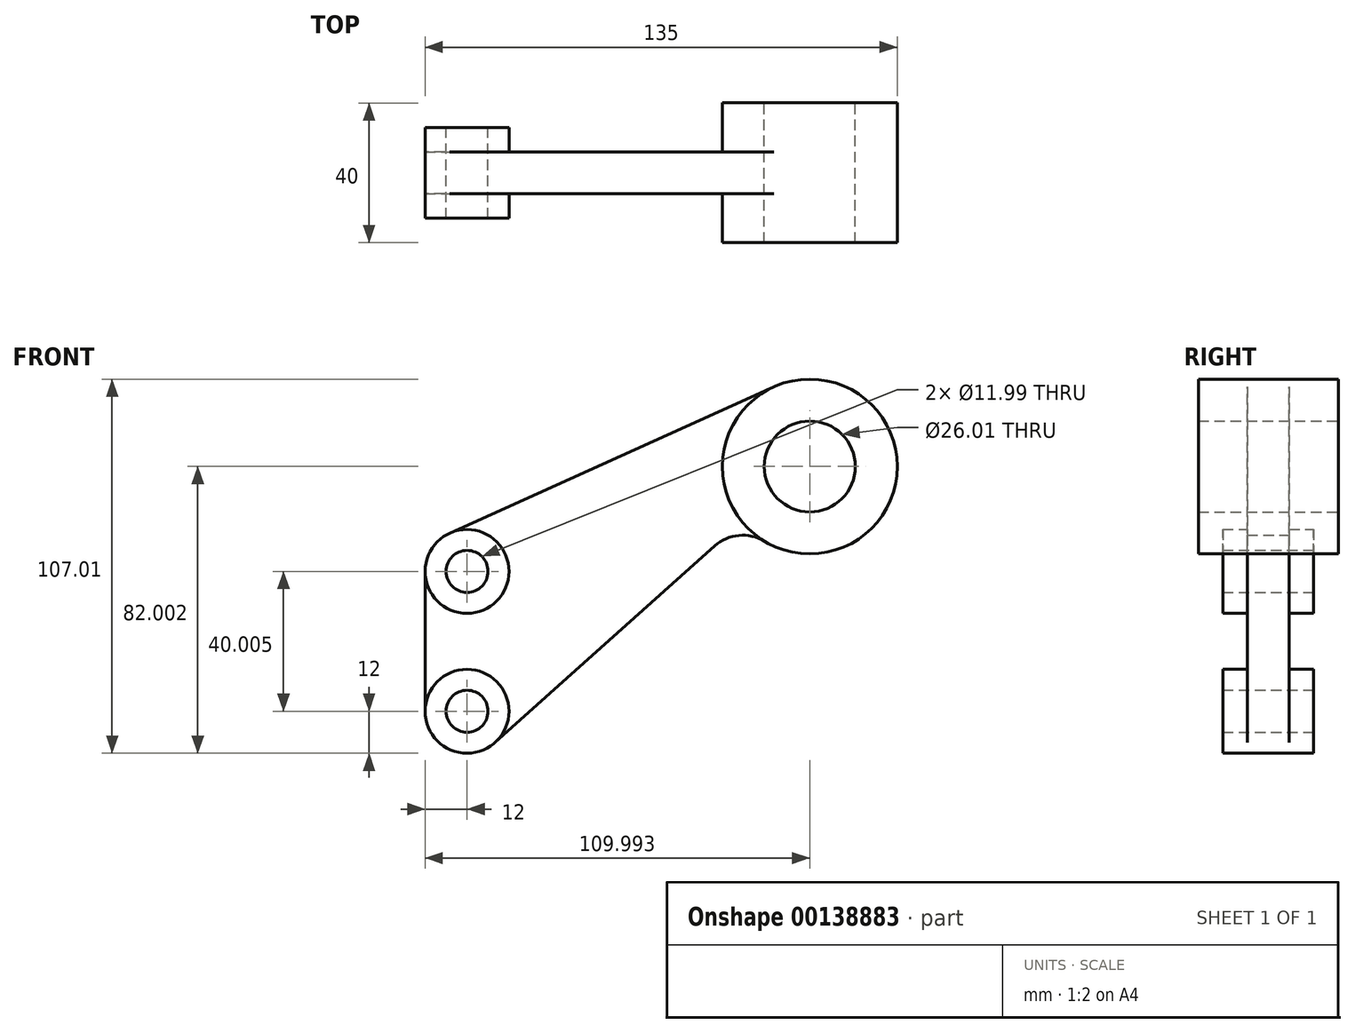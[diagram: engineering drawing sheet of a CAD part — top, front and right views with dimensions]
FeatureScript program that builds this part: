
annotation { "Feature Type Name" : "Feature", "Feature Type Description" : "" }
export const myFeature = defineFeature(function(context is Context, id is Id, definition is map)
    precondition{}
    {
        {
            var Q0;
            Q0=qCreatedBy(makeId("Front.planeOp"),FACE);
            var sketch = newSketch(context, id + "F0", { "sketchPlane" : qUnion([Q0])});
            skCircle(sketch, "E0", {"center": v(0, 0) * mm, "radius": 6 * mm});
            skCircle(sketch, "E1", {"center": v(0, 0) * mm, "radius": 12 * mm});
            skCircle(sketch, "E2", {"center": v(0, 40) * mm, "radius": 6 * mm});
            skCircle(sketch, "E3", {"center": v(0, 40) * mm, "radius": 12 * mm});
            skCircle(sketch, "E4", {"center": v(98, 70) * mm, "radius": 25 * mm});
            skCircle(sketch, "E5", {"center": v(98, 70) * mm, "radius": 13 * mm});
            skLineSegment(sketch, "E6", {"start": v(-12, 0) * mm, "end": v(-12, 40) * mm});
            skLineSegment(sketch, "E7", {"start": v(-4.94, 50.94) * mm, "end": v(87.7, 92.8) * mm});
            skLineSegment(sketch, "E8", {"start": v(8, -8.94) * mm, "end": v(70.84, 47.29) * mm});
            skArc(sketch, "E9", {"start": v(85.04, 48.61) * mm, "mid": v(77.72, 50.3) * mm, "end": v(70.84, 47.29) * mm});
            skSolve(sketch);
        }
        {
            var Q0;
            {var subQ0=sQuery(id+"F0.wireOp",EDGE,"E6");Q0=makeQuery(id+"F0.imprint","IMPRINT",FACE,{"disambiguationData":[TD([[makeQuery(id+"F0.imprint","IMPRINT",EDGE,{"derivedFrom":subQ0}),-1.0]])]});}
            extrude(context, id + "F1", {"entities" : qUnion([Q0]), "endBound" : BoundingType.SYMMETRIC, "depth" : 12 * mm});
        }
        {
            var Q0;
            Q0=makeQuery(id+"F0.imprint","IMPRINT",FACE,{"disambiguationData":[TD([[makeQuery(id+"F0.imprint","IMPRINT",EDGE,{"derivedFrom":sQuery(id+"F0.wireOp",EDGE,"E2")}),-1.0]])]});
            var Q1;
            Q1=makeQuery(id+"F0.imprint","IMPRINT",FACE,{"disambiguationData":[TD([[makeQuery(id+"F0.imprint","IMPRINT",EDGE,{"derivedFrom":sQuery(id+"F0.wireOp",EDGE,"E0")}),-1.0]])]});
            extrude(context, id + "F2", {"entities" : qUnion([Q0, Q1]), "operationType" : NewBodyOperationType.ADD, "endBound" : BoundingType.SYMMETRIC, "depth" : 26 * mm});
        }
        {
            var Q0;
            Q0=makeQuery(id+"F0.imprint","IMPRINT",FACE,{"disambiguationData":[TD([[makeQuery(id+"F0.imprint","IMPRINT",EDGE,{"derivedFrom":sQuery(id+"F0.wireOp",EDGE,"E5")}),-1.0]])]});
            extrude(context, id + "F3", {"entities" : qUnion([Q0]), "operationType" : NewBodyOperationType.ADD, "endBound" : BoundingType.SYMMETRIC, "depth" : 40 * mm});
        }
    });
